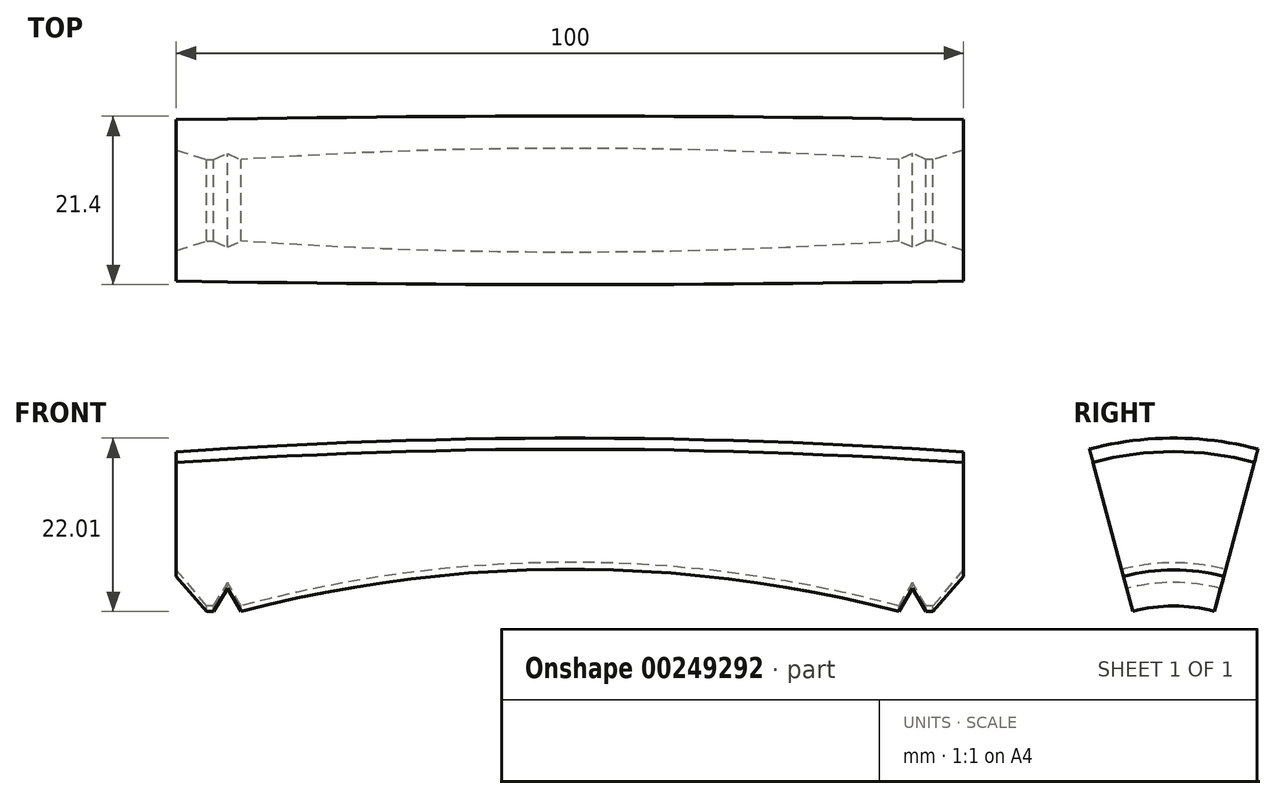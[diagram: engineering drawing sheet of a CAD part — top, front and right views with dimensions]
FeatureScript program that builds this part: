
annotation { "Feature Type Name" : "Feature", "Feature Type Description" : "" }
export const myFeature = defineFeature(function(context is Context, id is Id, definition is map)
    precondition{}
    {
        {
            var Q0;
            Q0=qCreatedBy(makeId("Front.planeOp"),FACE);
            var sketch = newSketch(context, id + "F0", { "sketchPlane" : qUnion([Q0])});
            skLineSegment(sketch, "E0", {"start": v(-45.06, 0) * mm, "end": v(40.19, 0) * mm, "construction": true});
            skLineSegment(sketch, "E1", {"start": v(-50, 39.6) * mm, "end": v(-43.46, 40) * mm});
            skLineSegment(sketch, "E2", {"start": v(43.46, 40) * mm, "end": v(50, 39.6) * mm});
            skLineSegment(sketch, "E3", {"start": v(-50, 39.6) * mm, "end": v(-50, 24.6) * mm});
            skLineSegment(sketch, "E4", {"start": v(-50, 24.6) * mm, "end": v(-46.14, 20) * mm});
            skLineSegment(sketch, "E5", {"start": v(-46.14, 20) * mm, "end": v(-45.23, 20) * mm});
            skLineSegment(sketch, "E6", {"start": v(50, 39.6) * mm, "end": v(50, 24.6) * mm});
            skLineSegment(sketch, "E7", {"start": v(50, 24.6) * mm, "end": v(46.14, 20) * mm});
            skLineSegment(sketch, "E8", {"start": v(46.14, 20) * mm, "end": v(45.23, 20) * mm});
            skLineSegment(sketch, "E9", {"start": v(-45.23, 20) * mm, "end": v(-43.5, 23) * mm});
            skLineSegment(sketch, "E10", {"start": v(-43.5, 23) * mm, "end": v(-41.77, 20) * mm});
            skLineSegment(sketch, "E11", {"start": v(45.23, 20) * mm, "end": v(43.5, 23) * mm});
            skLineSegment(sketch, "E12", {"start": v(43.5, 23) * mm, "end": v(41.77, 20) * mm});
            skArc(sketch, "E13", {"start": v(41.77, 20) * mm, "mid": v(0, 25.55) * mm, "end": v(-41.77, 20) * mm});
            skArc(sketch, "E14", {"start": v(43.46, 40) * mm, "mid": v(0, 41.33) * mm, "end": v(-43.46, 40) * mm});
            skSolve(sketch);
        }
        {
            var Q0;
            Q0=makeQuery(id+"F0.imprint","IMPRINT",FACE,{"disambiguationData":[TD([[makeQuery(id+"F0.imprint","IMPRINT",EDGE,{"derivedFrom":sQuery(id+"F0.wireOp",EDGE,"E1")}),-1.0]])]});
            var Q1;
            Q1=sQuery(id+"F0.wireOp",EDGE,"E0");
            revolve(context, id + "F1", {"surfaceOperationType" : NewSurfaceOperationType.NEW, "entities" : qUnion([Q0]), "axis" : qUnion([Q1]), "revolveType" : RevolveType.SYMMETRIC, "angle" : 30 * degree});
        }
    });
